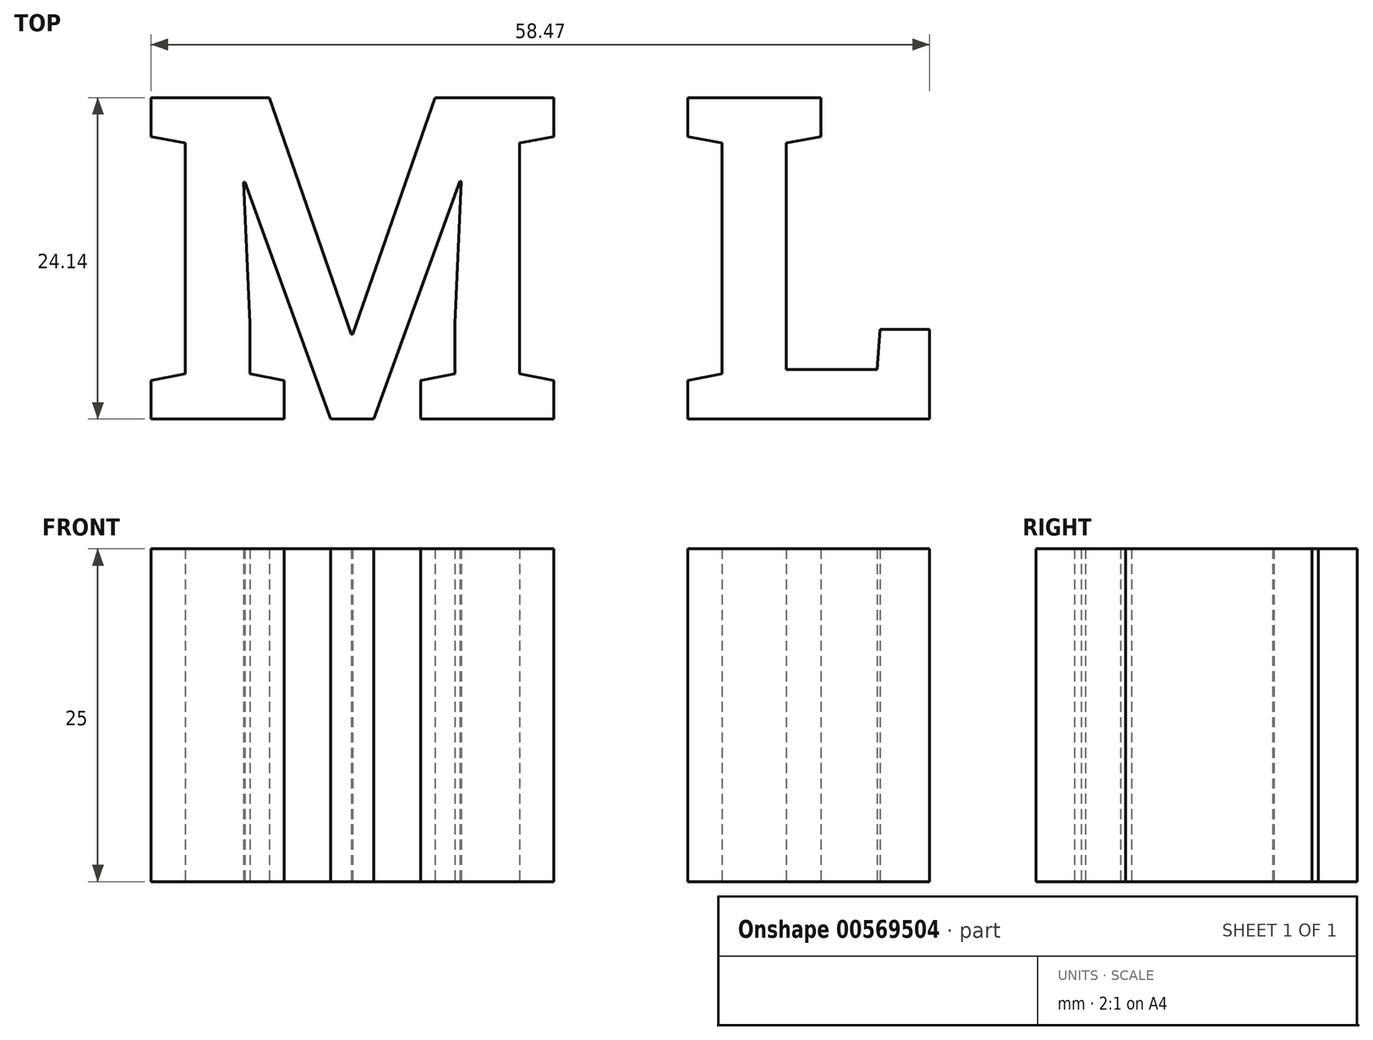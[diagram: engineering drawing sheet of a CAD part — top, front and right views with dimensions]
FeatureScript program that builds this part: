
annotation { "Feature Type Name" : "Feature", "Feature Type Description" : "" }
export const myFeature = defineFeature(function(context is Context, id is Id, definition is map)
    precondition{}
    {
        {
            var Q0;
            Q0=qCreatedBy(makeId("Top.planeOp"),FACE);
            var sketch = newSketch(context, id + "F0", { "sketchPlane" : qUnion([Q0])});
            skText(sketch, "E0", { "text": "M L", "fontName": "RobotoSlab-Bold.ttf"});
            const initialGuessF0  = {"E0": [-0.0232, -0.02108, 1, 0, 0.02445]};
            skSetInitialGuess(sketch, initialGuessF0);
            skSolve(sketch);
        }
        {
            var Q0;
            Q0 = qSketchRegion(id + "F0", true);
            extrude(context, id + "F1", {"entities" : qUnion([Q0]), "depth" : 25 * mm, "offsetDistance" : 25 * mm});
        }
    });
